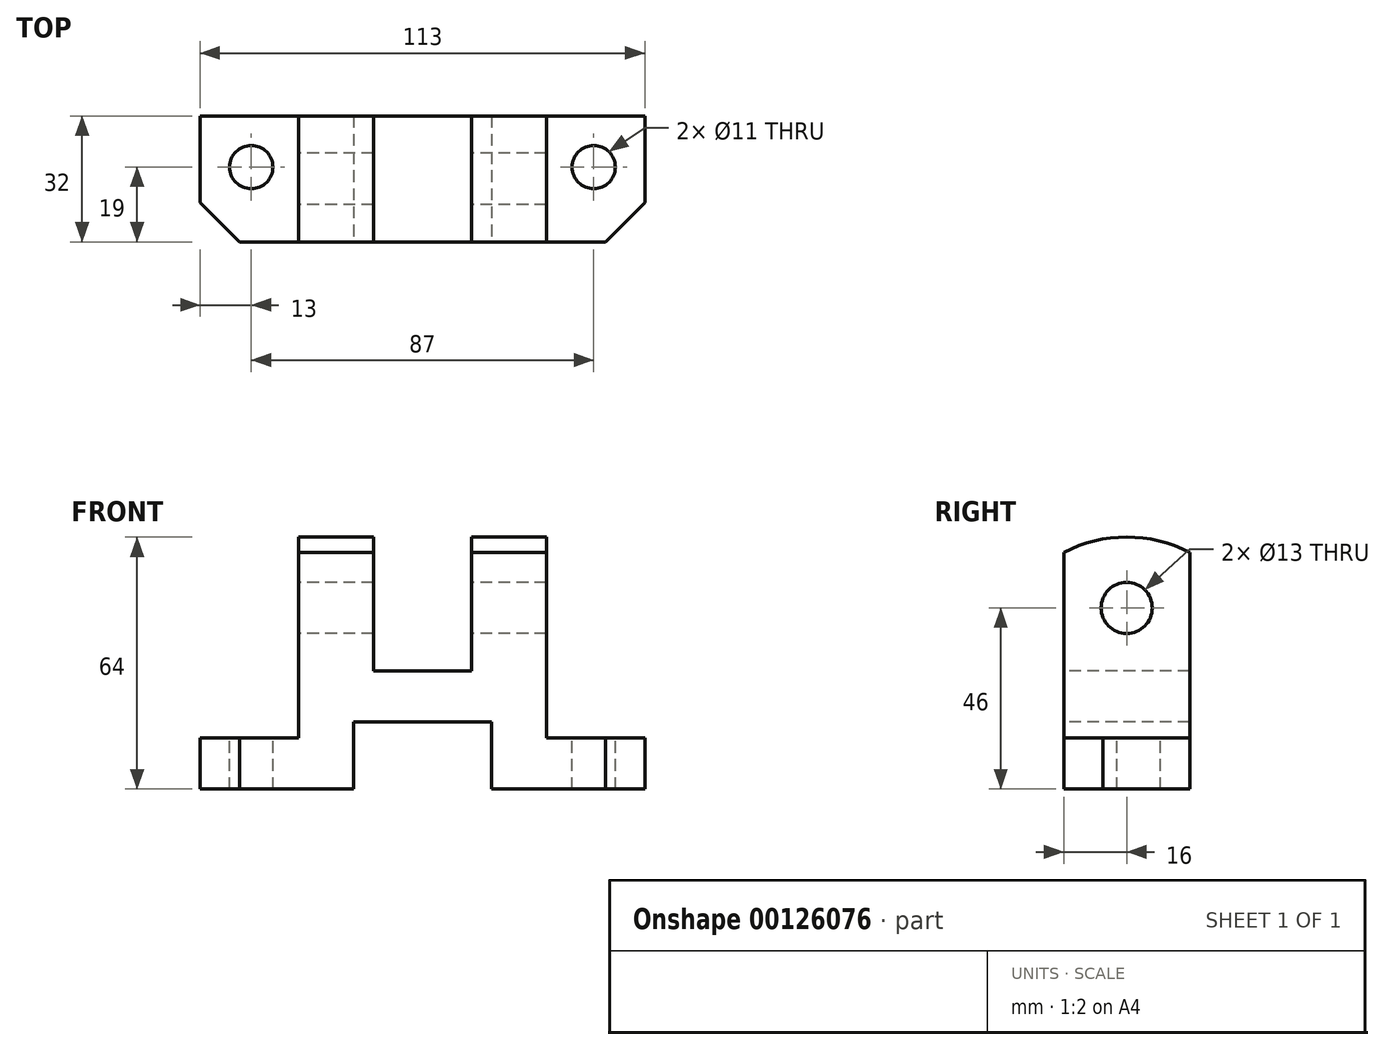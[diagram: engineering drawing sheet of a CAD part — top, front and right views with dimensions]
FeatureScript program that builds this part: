
annotation { "Feature Type Name" : "Feature", "Feature Type Description" : "" }
export const myFeature = defineFeature(function(context is Context, id is Id, definition is map)
    precondition{}
    {
        {
            var Q0;
            Q0=qCreatedBy(makeId("Right.planeOp"),FACE);
            var sketch = newSketch(context, id + "F0", { "sketchPlane" : qUnion([Q0])});
            skLineSegment(sketch, "E0", {"start": v(0, 0) * mm, "end": v(0, 60.13) * mm});
            skLineSegment(sketch, "E1", {"start": v(0, 0) * mm, "end": v(32, 0) * mm});
            skLineSegment(sketch, "E2", {"start": v(32, 0) * mm, "end": v(32, 60.13) * mm});
            skArc(sketch, "E3", {"start": v(32, 60.13) * mm, "mid": v(16, 64) * mm, "end": v(0, 60.13) * mm});
            skCircle(sketch, "E4", {"center": v(16, 46) * mm, "radius": 6.5 * mm});
            skSolve(sketch);
        }
        {
            var Q0;
            Q0 = qSketchRegion(id + "F0", true);
            extrude(context, id + "F1", {"entities" : qUnion([Q0]), "depth" : 113 * mm});
        }
        {
            var Q0;
            Q0=makeQuery(id+"F1.opExtrude","SWEPT_FACE",FACE,{"disambiguationData":[OSD([sQuery(id+"F0.wireOp",EDGE,"E0")])]});
            var sketch = newSketch(context, id + "F2", { "sketchPlane" : qUnion([Q0])});
            skLineSegment(sketch, "E5.bottom", {"start": v(39, 0) * mm, "end": v(74, 0) * mm});
            skLineSegment(sketch, "E5.top", {"start": v(39, 17) * mm, "end": v(74, 17) * mm});
            skLineSegment(sketch, "E5.left", {"start": v(39, 0) * mm, "end": v(39, 17) * mm});
            skLineSegment(sketch, "E5.right", {"start": v(74, 0) * mm, "end": v(74, 17) * mm});
            skLineSegment(sketch, "E6.bottom", {"start": v(88, 64) * mm, "end": v(113, 64) * mm});
            skLineSegment(sketch, "E6.top", {"start": v(88, 13) * mm, "end": v(113, 13) * mm});
            skLineSegment(sketch, "E6.left", {"start": v(88, 64) * mm, "end": v(88, 13) * mm});
            skLineSegment(sketch, "E6.right", {"start": v(113, 64) * mm, "end": v(113, 13) * mm});
            skLineSegment(sketch, "E7.bottom", {"start": v(25, 64) * mm, "end": v(0, 64) * mm});
            skLineSegment(sketch, "E7.top", {"start": v(25, 13) * mm, "end": v(0, 13) * mm});
            skLineSegment(sketch, "E7.left", {"start": v(25, 64) * mm, "end": v(25, 13) * mm});
            skLineSegment(sketch, "E7.right", {"start": v(0, 64) * mm, "end": v(0, 13) * mm});
            skLineSegment(sketch, "E8.bottom", {"start": v(44, 64) * mm, "end": v(69, 64) * mm});
            skLineSegment(sketch, "E8.top", {"start": v(44, 30) * mm, "end": v(69, 30) * mm});
            skLineSegment(sketch, "E8.left", {"start": v(44, 64) * mm, "end": v(44, 30) * mm});
            skLineSegment(sketch, "E8.right", {"start": v(69, 64) * mm, "end": v(69, 30) * mm});
            skSolve(sketch);
        }
        {
            var Q0;
            {var subQ0=sQuery(id+"F2.wireOp",EDGE,"E7.bottom");Q0=makeQuery(id+"F2.imprint","IMPRINT",FACE,{"disambiguationData":[TD([[makeQuery(id+"F2.imprint","IMPRINT",EDGE,{"derivedFrom":subQ0}),1.0]])]});}
            var Q1;
            {var subQ0=sQuery(id+"F2.wireOp",EDGE,"E7.top");Q1=makeQuery(id+"F2.imprint","IMPRINT",FACE,{"disambiguationData":[TD([[makeQuery(id+"F2.imprint","IMPRINT",EDGE,{"derivedFrom":subQ0}),-1.0]])]});}
            var Q2;
            {var subQ0=sQuery(id+"F2.wireOp",EDGE,"E8.top");Q2=makeQuery(id+"F2.imprint","IMPRINT",FACE,{"disambiguationData":[TD([[makeQuery(id+"F2.imprint","IMPRINT",EDGE,{"derivedFrom":subQ0}),1.0]])]});}
            var Q3;
            {var subQ0=sQuery(id+"F2.wireOp",EDGE,"E8.bottom");Q3=makeQuery(id+"F2.imprint","IMPRINT",FACE,{"disambiguationData":[TD([[makeQuery(id+"F2.imprint","IMPRINT",EDGE,{"derivedFrom":subQ0}),-1.0]])]});}
            var Q4;
            {var subQ0=sQuery(id+"F2.wireOp",EDGE,"E6.bottom");Q4=makeQuery(id+"F2.imprint","IMPRINT",FACE,{"disambiguationData":[TD([[makeQuery(id+"F2.imprint","IMPRINT",EDGE,{"derivedFrom":subQ0}),-1.0]])]});}
            var Q5;
            {var subQ0=sQuery(id+"F2.wireOp",EDGE,"E6.top");Q5=makeQuery(id+"F2.imprint","IMPRINT",FACE,{"disambiguationData":[TD([[makeQuery(id+"F2.imprint","IMPRINT",EDGE,{"derivedFrom":subQ0}),1.0]])]});}
            var Q6;
            Q6=makeQuery(id+"F2.imprint","IMPRINT",FACE,{"disambiguationData":[TD([[makeQuery(id+"F2.imprint","IMPRINT",EDGE,{"derivedFrom":sQuery(id+"F2.wireOp",EDGE,"E5.bottom")}),-1.0]])]});
            extrude(context, id + "F3", {"entities" : qUnion([Q0, Q1, Q2, Q3, Q4, Q5, Q6]), "operationType" : NewBodyOperationType.REMOVE, "endBound" : BoundingType.THROUGH_ALL, "oppositeDirection" : true, "depth" : 25 * mm});
        }
        {
            var Q0;
            Q0=makeQuery(id+"F3.boolean.opBoolean","COPY",FACE,{"derivedFrom":makeQuery(id+"F3.opExtrude","SWEPT_FACE",FACE,{"disambiguationData":[OSD([sQuery(id+"F2.wireOp",EDGE,"E6.top")])]})});
            var sketch = newSketch(context, id + "F4", { "sketchPlane" : qUnion([Q0])});
            skLineSegment(sketch, "E9", {"start": v(113, 0) * mm, "end": v(113, 10) * mm});
            skLineSegment(sketch, "E10", {"start": v(113, 10) * mm, "end": v(103, 0) * mm});
            skLineSegment(sketch, "E11", {"start": v(103, 0) * mm, "end": v(113, 0) * mm});
            skLineSegment(sketch, "E12", {"start": v(0, 0) * mm, "end": v(0, 10) * mm});
            skLineSegment(sketch, "E13", {"start": v(0, 10) * mm, "end": v(10, 0) * mm});
            skLineSegment(sketch, "E14", {"start": v(10, 0) * mm, "end": v(0, 0) * mm});
            skCircle(sketch, "E15", {"center": v(13, 19) * mm, "radius": 5.5 * mm});
            skCircle(sketch, "E16", {"center": v(100, 19) * mm, "radius": 5.5 * mm});
            skSolve(sketch);
        }
        {
            var Q0;
            Q0=makeQuery(id+"F4.imprint","IMPRINT",FACE,{"disambiguationData":[TD([[makeQuery(id+"F4.imprint","IMPRINT",EDGE,{"derivedFrom":sQuery(id+"F4.wireOp",EDGE,"E9")}),-1.0]])]});
            var Q1;
            Q1=makeQuery(id+"F4.imprint","IMPRINT",FACE,{"disambiguationData":[TD([[makeQuery(id+"F4.imprint","IMPRINT",EDGE,{"derivedFrom":sQuery(id+"F4.wireOp",EDGE,"E16")}),1.0]])]});
            var Q2;
            Q2=makeQuery(id+"F4.imprint","IMPRINT",FACE,{"disambiguationData":[TD([[makeQuery(id+"F4.imprint","IMPRINT",EDGE,{"derivedFrom":sQuery(id+"F4.wireOp",EDGE,"E15")}),1.0]])]});
            var Q3;
            Q3=makeQuery(id+"F4.imprint","IMPRINT",FACE,{"disambiguationData":[TD([[makeQuery(id+"F4.imprint","IMPRINT",EDGE,{"derivedFrom":sQuery(id+"F4.wireOp",EDGE,"E12")}),-1.0]])]});
            extrude(context, id + "F5", {"entities" : qUnion([Q0, Q1, Q2, Q3]), "operationType" : NewBodyOperationType.REMOVE, "endBound" : BoundingType.THROUGH_ALL, "oppositeDirection" : true, "depth" : 25 * mm});
        }
    });
